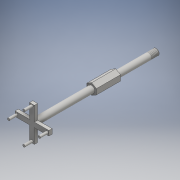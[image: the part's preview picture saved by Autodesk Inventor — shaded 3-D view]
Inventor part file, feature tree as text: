
AUTODESK INVENTOR PART (.ipt)
format: ipt  version: 2016 (Build 200138000, 138)  size: 141,824 bytes
history: native  units: mm
features: extrude x5, sketch x5, thread x1
ambient origin geometry x8: Origin, YZ Plane, XZ Plane, XY Plane, X Axis, Y Axis, Z Axis, Center Point
bodies: 实体1 (feature_tree)
feature tree (11):
  extrude  "拉伸1"  Depth=15.0mm
  extrude  "拉伸2"  Depth=5.0mm TaperAngle=0.0deg
  thread  "螺纹1"  [1 undecoded]
  extrude  "拉伸6"  Depth=35.0mm TaperAngle=0.0deg
  extrude  "拉伸7"  Depth=2.0mm TaperAngle=0.0deg
  extrude  "拉伸8"  Depth=5.0mm
  sketch  "草图1"  dims[d1=15.0mm d2=0.0mm d3=3.9mm]
  sketch  "草图2"  dims[d4=25.0mm d5=0.0mm d6=5.0mm d7=0.0mm d12=4.0mm]
  sketch  "草图6"  dims[d22=4.0mm d23=35.0mm d24=0.0mm]
  sketch  "草图7"  dims[d25=3.0mm d26=21.0mm d27=2.0mm d28=0.0mm]
  sketch  "草图8"  dims[d29=19.0mm d30=1.5mm d31=1.5mm d32=1.5mm d33=1.5mm d34=5.0mm d35=0.0mm]
note: 1 required parameter value undecoded (feature->parameter linkage not recoverable at this tier; creation-order binding heuristic only, values carry confidence <= 0.55)
